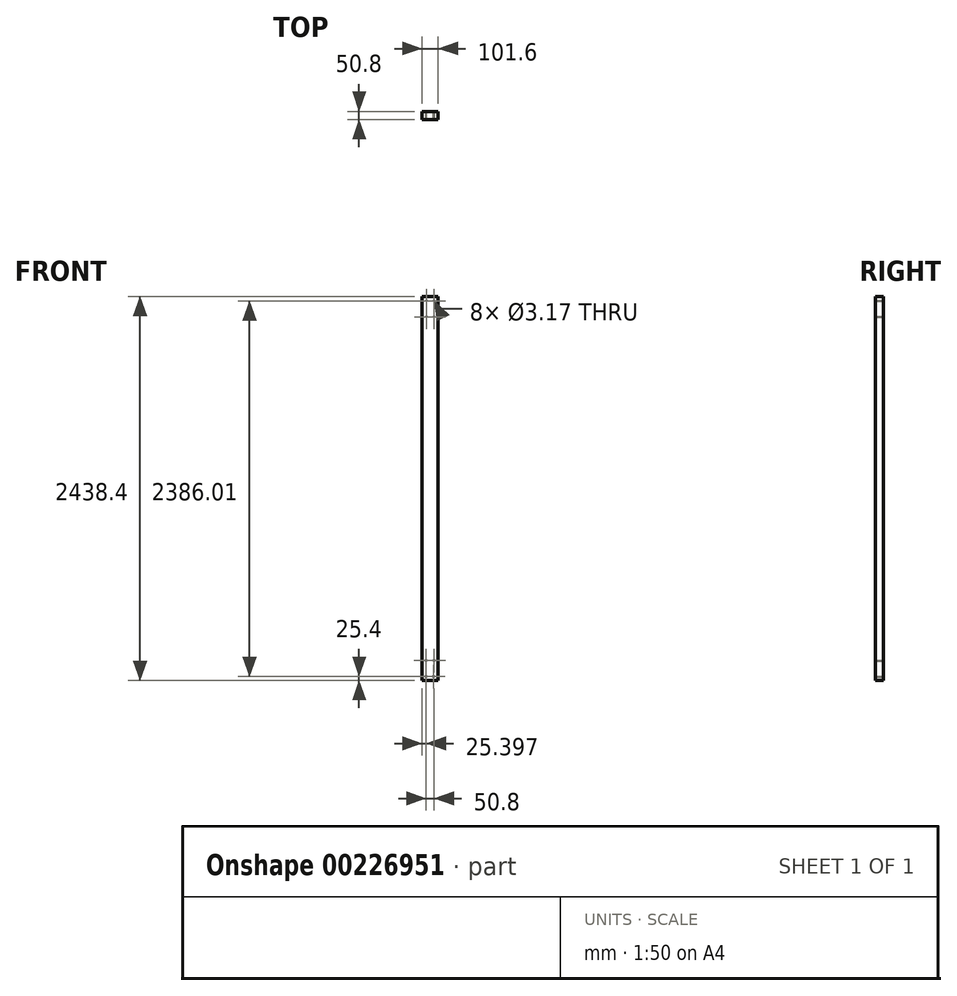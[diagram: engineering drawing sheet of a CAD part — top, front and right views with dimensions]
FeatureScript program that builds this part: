
annotation { "Feature Type Name" : "Feature", "Feature Type Description" : "" }
export const myFeature = defineFeature(function(context is Context, id is Id, definition is map)
    precondition{}
    {
        {
            var Q0;
            Q0=qCreatedBy(makeId("Front.planeOp"),FACE);
            var sketch = newSketch(context, id + "F0", { "sketchPlane" : qUnion([Q0])});
            skLineSegment(sketch, "E0", {"start": v(-48.78, 2413) * mm, "end": v(52.82, 2413) * mm});
            skLineSegment(sketch, "E1", {"start": v(-48.78, 2413) * mm, "end": v(-48.78, -25.4) * mm});
            skLineSegment(sketch, "E2", {"start": v(52.82, 2413) * mm, "end": v(52.82, -25.4) * mm});
            skLineSegment(sketch, "E3", {"start": v(52.82, -25.4) * mm, "end": v(-48.78, -25.4) * mm});
            skCircle(sketch, "E4", {"center": v(-21.8, 2386.01) * mm, "radius": 1.59 * mm});
            skCircle(sketch, "E5", {"center": v(25.83, 2386.01) * mm, "radius": 1.59 * mm});
            skCircle(sketch, "E6", {"center": v(25.83, 2284.41) * mm, "radius": 1.59 * mm});
            skCircle(sketch, "E7", {"center": v(-21.8, 2284.41) * mm, "radius": 1.59 * mm});
            skCircle(sketch, "E8", {"center": v(-23.38, 0) * mm, "radius": 1.59 * mm});
            skCircle(sketch, "E9", {"center": v(24.18, 0) * mm, "radius": 1.59 * mm});
            skCircle(sketch, "E10", {"center": v(-23.38, 101.6) * mm, "radius": 1.59 * mm});
            skCircle(sketch, "E11", {"center": v(27.42, 101.6) * mm, "radius": 1.59 * mm});
            skSolve(sketch);
        }
        {
            var Q0;
            Q0 = qSketchRegion(id + "F0", true);
            extrude(context, id + "F1", {"entities" : qUnion([Q0]), "depth" : 50.8 * mm});
        }
    });
